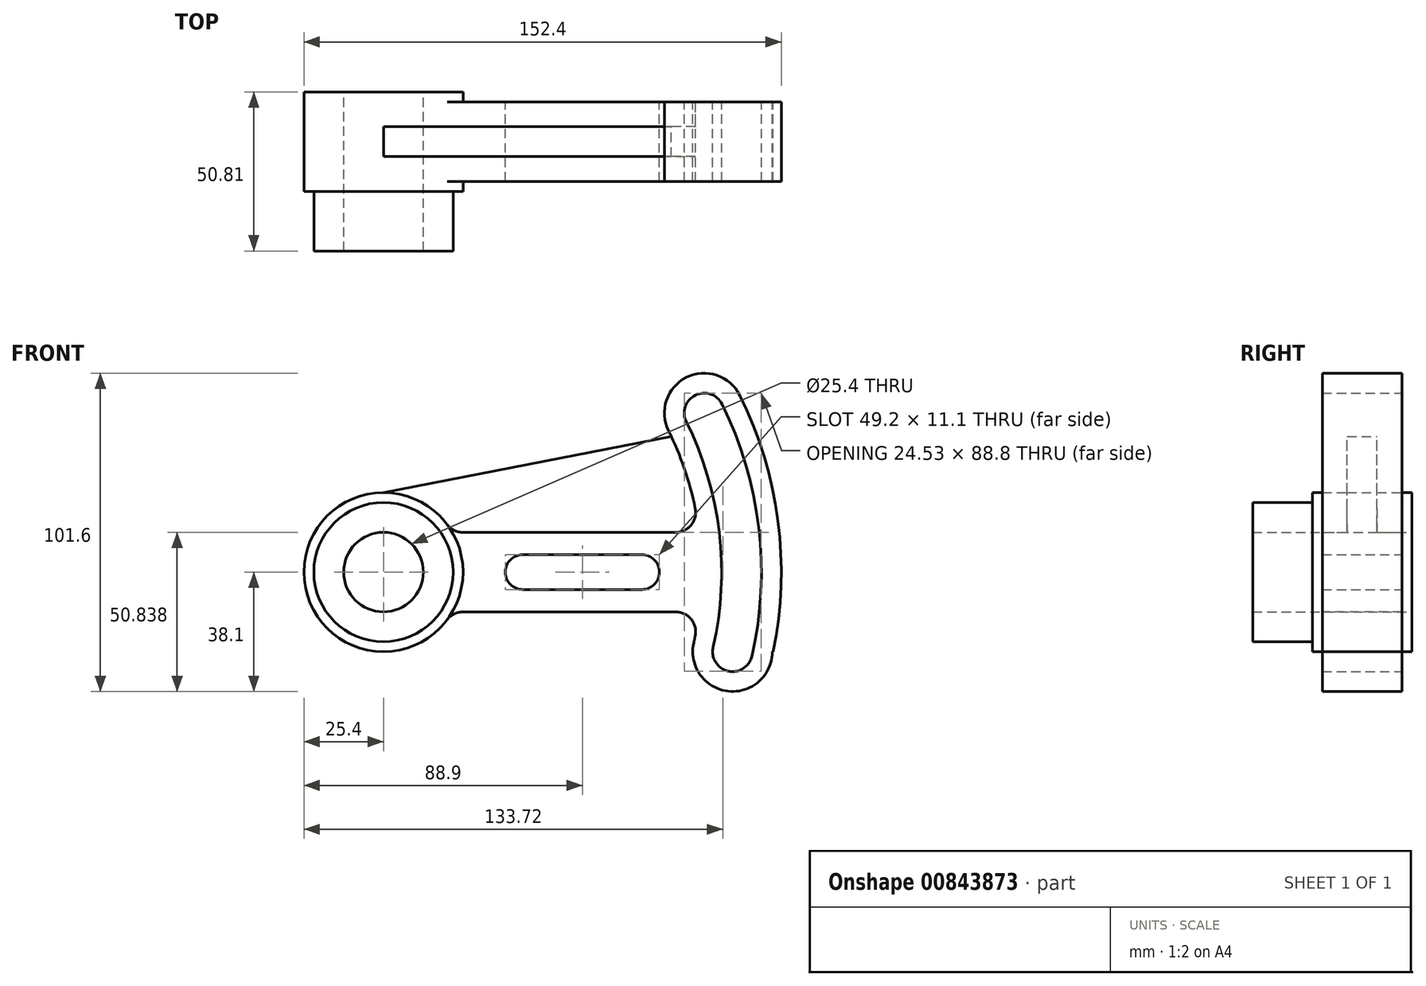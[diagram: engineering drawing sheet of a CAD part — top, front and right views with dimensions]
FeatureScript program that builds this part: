
annotation { "Feature Type Name" : "Feature", "Feature Type Description" : "" }
export const myFeature = defineFeature(function(context is Context, id is Id, definition is map)
    precondition{}
    {
        {
            var Q0;
            Q0=qCreatedBy(makeId("Front.planeOp"),FACE);
            var sketch = newSketch(context, id + "F0", { "sketchPlane" : qUnion([Q0])});
            skLineSegment(sketch, "E0", {"start": v(0, 0) * mm, "end": v(44.45, 0) * mm});
            skLineSegment(sketch, "E1", {"start": v(44.45, 0) * mm, "end": v(82.55, 0) * mm});
            skLineSegment(sketch, "E2", {"start": v(82.55, 0) * mm, "end": v(82.55, 12.7) * mm});
            skLineSegment(sketch, "E3", {"start": v(82.55, 0) * mm, "end": v(82.55, -12.7) * mm});
            skLineSegment(sketch, "E4", {"start": v(44.45, 0) * mm, "end": v(44.45, 12.7) * mm});
            skLineSegment(sketch, "E5", {"start": v(44.45, 0) * mm, "end": v(44.45, -12.7) * mm});
            skLineSegment(sketch, "E6", {"start": v(44.45, -12.7) * mm, "end": v(82.55, -12.7) * mm});
            skLineSegment(sketch, "E7", {"start": v(44.45, 12.7) * mm, "end": v(82.55, 12.7) * mm});
            skCircle(sketch, "E8", {"center": v(0, 0) * mm, "radius": 12.7 * mm});
            skArc(sketch, "E9", {"start": v(111.44, -25.4) * mm, "mid": v(113.5, 13.48) * mm, "end": v(102.4, 50.8) * mm});
            skLineSegment(sketch, "E10", {"start": v(82.55, 0) * mm, "end": v(135.94, 0) * mm});
            skLineSegment(sketch, "E11", {"start": v(135.94, 0) * mm, "end": v(135.94, -25.4) * mm});
            skLineSegment(sketch, "E12", {"start": v(135.94, -25.4) * mm, "end": v(111.44, -25.4) * mm});
            skLineSegment(sketch, "E13", {"start": v(135.94, 0) * mm, "end": v(135.94, 50.8) * mm});
            skLineSegment(sketch, "E14", {"start": v(135.94, 50.8) * mm, "end": v(102.4, 50.8) * mm});
            skCircle(sketch, "E15", {"center": v(102.4, 50.8) * mm, "radius": 6.35 * mm});
            skCircle(sketch, "E16", {"center": v(102.4, 50.8) * mm, "radius": 12.7 * mm});
            skCircle(sketch, "E17", {"center": v(111.44, -25.4) * mm, "radius": 6.35 * mm});
            skCircle(sketch, "E18", {"center": v(111.44, -25.4) * mm, "radius": 12.7 * mm});
            skPoint(sketch, "E19.start.orphan", {"position": v(0, 12.7) * mm});
            skCircle(sketch, "E20", {"center": v(0, 0) * mm, "radius": 22.23 * mm});
            skCircle(sketch, "E21", {"center": v(0, 0) * mm, "radius": 25.4 * mm});
            skLineSegment(sketch, "E22", {"start": v(0, 25.4) * mm, "end": v(91.93, 43.27) * mm});
            skLineSegment(sketch, "E23", {"start": v(44.45, 12.7) * mm, "end": v(22, 12.7) * mm});
            skArc(sketch, "E24", {"start": v(123.82, -28.22) * mm, "mid": v(126.11, 14.98) * mm, "end": v(113.77, 56.44) * mm});
            skArc(sketch, "E25", {"start": v(99.06, -22.58) * mm, "mid": v(100.9, 11.98) * mm, "end": v(91.01, 45.16) * mm});
            skArc(sketch, "E26", {"start": v(105.25, -23.99) * mm, "mid": v(107.2, 12.73) * mm, "end": v(96.7, 47.98) * mm});
            skArc(sketch, "E27", {"start": v(117.63, -26.81) * mm, "mid": v(119.8, 14.23) * mm, "end": v(108.08, 53.62) * mm});
            skLineSegment(sketch, "E28", {"start": v(44.45, -12.7) * mm, "end": v(22, -12.7) * mm});
            skLineSegment(sketch, "E29", {"start": v(82.55, -12.7) * mm, "end": v(100.8, -12.7) * mm});
            skLineSegment(sketch, "E30", {"start": v(82.55, 12.7) * mm, "end": v(100.8, 12.7) * mm});
            skCircle(sketch, "E31", {"center": v(44.45, 0) * mm, "radius": 5.55 * mm});
            skPoint(sketch, "E32.end.orphan", {"position": v(82.55, -6.35) * mm});
            skPoint(sketch, "E32.start.orphan", {"position": v(44.45, -6.35) * mm});
            skPoint(sketch, "E33.end.orphan", {"position": v(82.55, 6.35) * mm});
            skPoint(sketch, "E33.start.orphan", {"position": v(44.45, 6.35) * mm});
            skCircle(sketch, "E34", {"center": v(82.55, 0) * mm, "radius": 5.55 * mm});
            skLineSegment(sketch, "E35", {"start": v(44.45, 5.55) * mm, "end": v(82.55, 5.55) * mm});
            skLineSegment(sketch, "E36", {"start": v(44.45, -5.55) * mm, "end": v(82.55, -5.55) * mm});
            skSolve(sketch);
        }
        {
            var Q0;
            {var subQ0=sQuery(id+"F0.wireOp",EDGE,"E16");var subQ3=sQuery(id+"F0.wireOp",EDGE,"E14");var subQ4=makeQuery(id+"F0.imprint","INTERSECT",VERTEX,{"derivedFrom":[subQ3,subQ0]});Q0=makeQuery(id+"F0.imprint","IMPRINT",FACE,{"disambiguationData":[TD([[makeQuery(id+"F0.imprint","IMPRINT",EDGE,{"disambiguationData":[TD([[subQ4,-1.0]])],"derivedFrom":subQ3}),-1.0]])]});}
            var Q1;
            {var subQ0=sQuery(id+"F0.wireOp",EDGE,"E25");var subQ7=sQuery(id+"F0.wireOp",EDGE,"E10");var subQ8=makeQuery(id+"F0.imprint","INTERSECT",VERTEX,{"derivedFrom":[subQ7,subQ0]});Q1=makeQuery(id+"F0.imprint","IMPRINT",FACE,{"disambiguationData":[TD([[makeQuery(id+"F0.imprint","IMPRINT",EDGE,{"disambiguationData":[TD([[subQ8,-1.0]])],"derivedFrom":subQ7}),1.0]])]});}
            var Q2;
            {var subQ0=sQuery(id+"F0.wireOp",EDGE,"E25");var subQ4=sQuery(id+"F0.wireOp",EDGE,"E10");var subQ5=makeQuery(id+"F0.imprint","INTERSECT",VERTEX,{"derivedFrom":[subQ4,subQ0]});Q2=makeQuery(id+"F0.imprint","IMPRINT",FACE,{"disambiguationData":[TD([[makeQuery(id+"F0.imprint","IMPRINT",EDGE,{"disambiguationData":[TD([[subQ5,-1.0]])],"derivedFrom":subQ4}),-1.0]])]});}
            var Q3;
            {var subQ3=sQuery(id+"F0.wireOp",EDGE,"E10");var subQ7=sQuery(id+"F0.wireOp",EDGE,"E27");var subQ9=makeQuery(id+"F0.imprint","INTERSECT",VERTEX,{"derivedFrom":[subQ3,subQ7]});Q3=makeQuery(id+"F0.imprint","IMPRINT",FACE,{"disambiguationData":[TD([[makeQuery(id+"F0.imprint","IMPRINT",EDGE,{"disambiguationData":[TD([[subQ9,-1.0]])],"derivedFrom":subQ3}),-1.0]])]});}
            var Q4;
            {var subQ3=sQuery(id+"F0.wireOp",EDGE,"E10");var subQ7=sQuery(id+"F0.wireOp",EDGE,"E27");var subQ9=makeQuery(id+"F0.imprint","INTERSECT",VERTEX,{"derivedFrom":[subQ3,subQ7]});Q4=makeQuery(id+"F0.imprint","IMPRINT",FACE,{"disambiguationData":[TD([[makeQuery(id+"F0.imprint","IMPRINT",EDGE,{"disambiguationData":[TD([[subQ9,-1.0]])],"derivedFrom":subQ3}),1.0]])]});}
            var Q5;
            {var subQ0=sQuery(id+"F0.wireOp",EDGE,"E18");var subQ1=sQuery(id+"F0.wireOp",EDGE,"E12");var subQ2=makeQuery(id+"F0.imprint","INTERSECT",VERTEX,{"derivedFrom":[subQ1,subQ0]});Q5=makeQuery(id+"F0.imprint","IMPRINT",FACE,{"disambiguationData":[TD([[makeQuery(id+"F0.imprint","IMPRINT",EDGE,{"disambiguationData":[TD([[subQ2,-1.0]])],"derivedFrom":subQ1}),-1.0]])]});}
            var Q6;
            {var subQ0=sQuery(id+"F0.wireOp",EDGE,"E18");var subQ6=sQuery(id+"F0.wireOp",EDGE,"E12");var subQ11=makeQuery(id+"F0.imprint","INTERSECT",VERTEX,{"derivedFrom":[subQ6,subQ0]});Q6=makeQuery(id+"F0.imprint","IMPRINT",FACE,{"disambiguationData":[TD([[makeQuery(id+"F0.imprint","IMPRINT",EDGE,{"disambiguationData":[TD([[subQ11,-1.0]])],"derivedFrom":subQ6}),1.0]])]});}
            var Q7;
            {var subQ0=sQuery(id+"F0.wireOp",EDGE,"E16");var subQ1=sQuery(id+"F0.wireOp",EDGE,"E14");var subQ2=makeQuery(id+"F0.imprint","INTERSECT",VERTEX,{"derivedFrom":[subQ1,subQ0]});Q7=makeQuery(id+"F0.imprint","IMPRINT",FACE,{"disambiguationData":[TD([[makeQuery(id+"F0.imprint","IMPRINT",EDGE,{"disambiguationData":[TD([[subQ2,-1.0]])],"derivedFrom":subQ1}),1.0]])]});}
            var Q8;
            {var subQ0=sQuery(id+"F0.wireOp",EDGE,"E24");var subQ1=sQuery(id+"F0.wireOp",EDGE,"E14");var subQ2=makeQuery(id+"F0.imprint","INTERSECT",VERTEX,{"derivedFrom":[subQ1,subQ0]});Q8=makeQuery(id+"F0.imprint","IMPRINT",FACE,{"disambiguationData":[TD([[makeQuery(id+"F0.imprint","IMPRINT",EDGE,{"disambiguationData":[TD([[subQ2,-1.0]])],"derivedFrom":subQ1}),-1.0]])]});}
            var Q9;
            {var subQ0=sQuery(id+"F0.wireOp",EDGE,"E23");Q9=makeQuery(id+"F0.imprint","IMPRINT",FACE,{"disambiguationData":[TD([[makeQuery(id+"F0.imprint","IMPRINT",EDGE,{"derivedFrom":subQ0}),1.0]])]});}
            var Q10;
            {var subQ0=sQuery(id+"F0.wireOp",EDGE,"E7");Q10=makeQuery(id+"F0.imprint","IMPRINT",FACE,{"disambiguationData":[TD([[makeQuery(id+"F0.imprint","IMPRINT",EDGE,{"derivedFrom":subQ0}),-1.0]])]});}
            var Q11;
            {var subQ0=sQuery(id+"F0.wireOp",EDGE,"E30");Q11=makeQuery(id+"F0.imprint","IMPRINT",FACE,{"disambiguationData":[TD([[makeQuery(id+"F0.imprint","IMPRINT",EDGE,{"derivedFrom":subQ0}),-1.0]])]});}
            var Q12;
            {var subQ0=sQuery(id+"F0.wireOp",EDGE,"E29");Q12=makeQuery(id+"F0.imprint","IMPRINT",FACE,{"disambiguationData":[TD([[makeQuery(id+"F0.imprint","IMPRINT",EDGE,{"derivedFrom":subQ0}),1.0]])]});}
            var Q13;
            {var subQ0=sQuery(id+"F0.wireOp",EDGE,"E6");Q13=makeQuery(id+"F0.imprint","IMPRINT",FACE,{"disambiguationData":[TD([[makeQuery(id+"F0.imprint","IMPRINT",EDGE,{"derivedFrom":subQ0}),1.0]])]});}
            var Q14;
            {var subQ5=sQuery(id+"F0.wireOp",EDGE,"E28");Q14=makeQuery(id+"F0.imprint","IMPRINT",FACE,{"disambiguationData":[TD([[makeQuery(id+"F0.imprint","IMPRINT",EDGE,{"derivedFrom":subQ5}),-1.0]])]});}
            var Q15;
            Q15=makeQuery(id+"F0.imprint","IMPRINT",FACE,{"disambiguationData":[TD([[makeQuery(id+"F0.imprint","IMPRINT",EDGE,{"derivedFrom":sQuery(id+"F0.wireOp",EDGE,"E20")}),-1.0]])]});
            var Q16;
            Q16=makeQuery(id+"F0.imprint","IMPRINT",FACE,{"disambiguationData":[TD([[makeQuery(id+"F0.imprint","IMPRINT",EDGE,{"derivedFrom":sQuery(id+"F0.wireOp",EDGE,"E8")}),-1.0]])]});
            extrude(context, id + "F1", {"entities" : qUnion([Q0, Q1, Q2, Q3, Q4, Q5, Q6, Q7, Q8, Q9, Q10, Q11, Q12, Q13, Q14, Q15, Q16]), "depth" : 12.7 * mm, "offsetDistance" : 25.4 * mm});
        }
        {
            var Q0;
            Q0=makeQuery(id+"F0.imprint","IMPRINT",FACE,{"disambiguationData":[TD([[makeQuery(id+"F0.imprint","IMPRINT",EDGE,{"derivedFrom":sQuery(id+"F0.wireOp",EDGE,"E8")}),-1.0]])]});
            var Q1;
            Q1=makeQuery(id+"F0.imprint","IMPRINT",FACE,{"disambiguationData":[TD([[makeQuery(id+"F0.imprint","IMPRINT",EDGE,{"derivedFrom":sQuery(id+"F0.wireOp",EDGE,"E20")}),-1.0]])]});
            extrude(context, id + "F2", {"entities" : qUnion([Q0, Q1]), "operationType" : NewBodyOperationType.ADD, "depth" : 15.88 * mm, "offsetDistance" : 25.4 * mm});
        }
        {
            var Q0;
            Q0=makeQuery(id+"F0.imprint","IMPRINT",FACE,{"disambiguationData":[TD([[makeQuery(id+"F0.imprint","IMPRINT",EDGE,{"derivedFrom":sQuery(id+"F0.wireOp",EDGE,"E7")}),1.0]])]});
            extrude(context, id + "F3", {"entities" : qUnion([Q0]), "operationType" : NewBodyOperationType.ADD, "depth" : 4.76 * mm, "offsetDistance" : 25.4 * mm});
        }
        {
            var Q0;
            Q0=makeQuery(id+"F1.opExtrude","SWEPT_BODY",BODY,{"disambiguationData":[OSD([sQuery(id+"F0.wireOp",EDGE,"E6"),sQuery(id+"F0.wireOp",EDGE,"E7"),sQuery(id+"F0.wireOp",EDGE,"k4cJhjc4-1s8r-fBwY-ps0i-m6zyavDnIOTd"),sQuery(id+"F0.wireOp",EDGE,"v0h4e1i3-Oo7c-5lFI-QYjD-X1nICo4Oxu65"),sQuery(id+"F0.wireOp",EDGE,"E32"),sQuery(id+"F0.wireOp",EDGE,"E33"),sQuery(id+"F0.wireOp",EDGE,"E8"),sQuery(id+"F0.wireOp",EDGE,"E12"),sQuery(id+"F0.wireOp",EDGE,"E15"),sQuery(id+"F0.wireOp",EDGE,"E16"),sQuery(id+"F0.wireOp",EDGE,"E17"),sQuery(id+"F0.wireOp",EDGE,"E18"),sQuery(id+"F0.wireOp",EDGE,"E21"),sQuery(id+"F0.wireOp",EDGE,"E23"),sQuery(id+"F0.wireOp",EDGE,"E24"),sQuery(id+"F0.wireOp",EDGE,"E25"),sQuery(id+"F0.wireOp",EDGE,"E26"),sQuery(id+"F0.wireOp",EDGE,"E27"),sQuery(id+"F0.wireOp",EDGE,"E28"),sQuery(id+"F0.wireOp",EDGE,"E29"),sQuery(id+"F0.wireOp",EDGE,"E30")])]});
            var Q1;
            Q1=makeQuery(id+"F0.imprint","IMPRINT",FACE,{"disambiguationData":[TD([[makeQuery(id+"F0.imprint","IMPRINT",EDGE,{"derivedFrom":sQuery(id+"F0.wireOp",EDGE,"E7")}),1.0]])]});
            mirror(context, id + "F4", {"operationType" : NewBodyOperationType.ADD, "entities" : qUnion([Q0]), "mirrorPlane" : qUnion([Q1])});
        }
        {
            var Q0;
            Q0=makeQuery(id+"F0.imprint","IMPRINT",FACE,{"disambiguationData":[TD([[makeQuery(id+"F0.imprint","IMPRINT",EDGE,{"derivedFrom":sQuery(id+"F0.wireOp",EDGE,"E8")}),-1.0]])]});
            extrude(context, id + "F5", {"entities" : qUnion([Q0]), "operationType" : NewBodyOperationType.ADD, "depth" : 34.92 * mm, "offsetDistance" : 25.4 * mm});
        }
        {
            var Q0;
            {var subQ0=makeQuery(id+"F3.opExtrude","SWEPT_EDGE",EDGE,{"disambiguationData":[OSD([sQuery(id+"F0.wireOp",EDGE,"E22"),sQuery(id+"F0.wireOp",EDGE,"E25")])]});Q0=makeQuery(id+"F4.boolean.opBoolean","MERGE",EDGE,{"derivedFrom":[subQ0,makeQuery(id+"F4.opPattern","COPY",EDGE,{"derivedFrom":subQ0,"instanceName":"1"})]});}
            var Q1;
            {var subQ0=makeQuery(id+"F1.opExtrude","SWEPT_EDGE",EDGE,{"disambiguationData":[OSD([sQuery(id+"F0.wireOp",EDGE,"E25"),sQuery(id+"F0.wireOp",EDGE,"E29")])]});Q1=makeQuery(id+"F4.boolean.opBoolean","MERGE",EDGE,{"derivedFrom":[subQ0,makeQuery(id+"F4.opPattern","COPY",EDGE,{"derivedFrom":subQ0,"instanceName":"1"})]});}
            var Q2;
            {var subQ0=makeQuery(id+"F1.opExtrude","SWEPT_EDGE",EDGE,{"disambiguationData":[OSD([sQuery(id+"F0.wireOp",EDGE,"E21"),sQuery(id+"F0.wireOp",EDGE,"E28")])]});Q2=makeQuery(id+"F4.boolean.opBoolean","MERGE",EDGE,{"derivedFrom":[subQ0,makeQuery(id+"F4.opPattern","COPY",EDGE,{"derivedFrom":subQ0,"instanceName":"1"})]});}
            var Q3;
            Q3=makeQuery(id+"F1.opExtrude","SWEPT_EDGE",EDGE,{"disambiguationData":[OSD([sQuery(id+"F0.wireOp",EDGE,"E21"),sQuery(id+"F0.wireOp",EDGE,"E23")])]});
            var Q4;
            Q4=makeQuery(id+"F4.opPattern","COPY",EDGE,{"derivedFrom":makeQuery(id+"F1.opExtrude","SWEPT_EDGE",EDGE,{"disambiguationData":[OSD([sQuery(id+"F0.wireOp",EDGE,"E21"),sQuery(id+"F0.wireOp",EDGE,"E23")])]}),"instanceName":"1"});
            var Q5;
            Q5=makeQuery(id+"F1.opExtrude","SWEPT_EDGE",EDGE,{"disambiguationData":[OSD([sQuery(id+"F0.wireOp",EDGE,"E25"),sQuery(id+"F0.wireOp",EDGE,"E30")])]});
            var Q6;
            Q6=makeQuery(id+"F4.opPattern","COPY",EDGE,{"derivedFrom":makeQuery(id+"F1.opExtrude","SWEPT_EDGE",EDGE,{"disambiguationData":[OSD([sQuery(id+"F0.wireOp",EDGE,"E25"),sQuery(id+"F0.wireOp",EDGE,"E30")])]}),"instanceName":"1"});
            fillet(context, id + "F6", {"entities" : qUnion([Q0, Q1, Q2, Q3, Q4, Q5, Q6]), "radius" : 6.35 * mm, "tangentPropagation" : true, "allowEdgeOverflow" : false});
        }
    });
